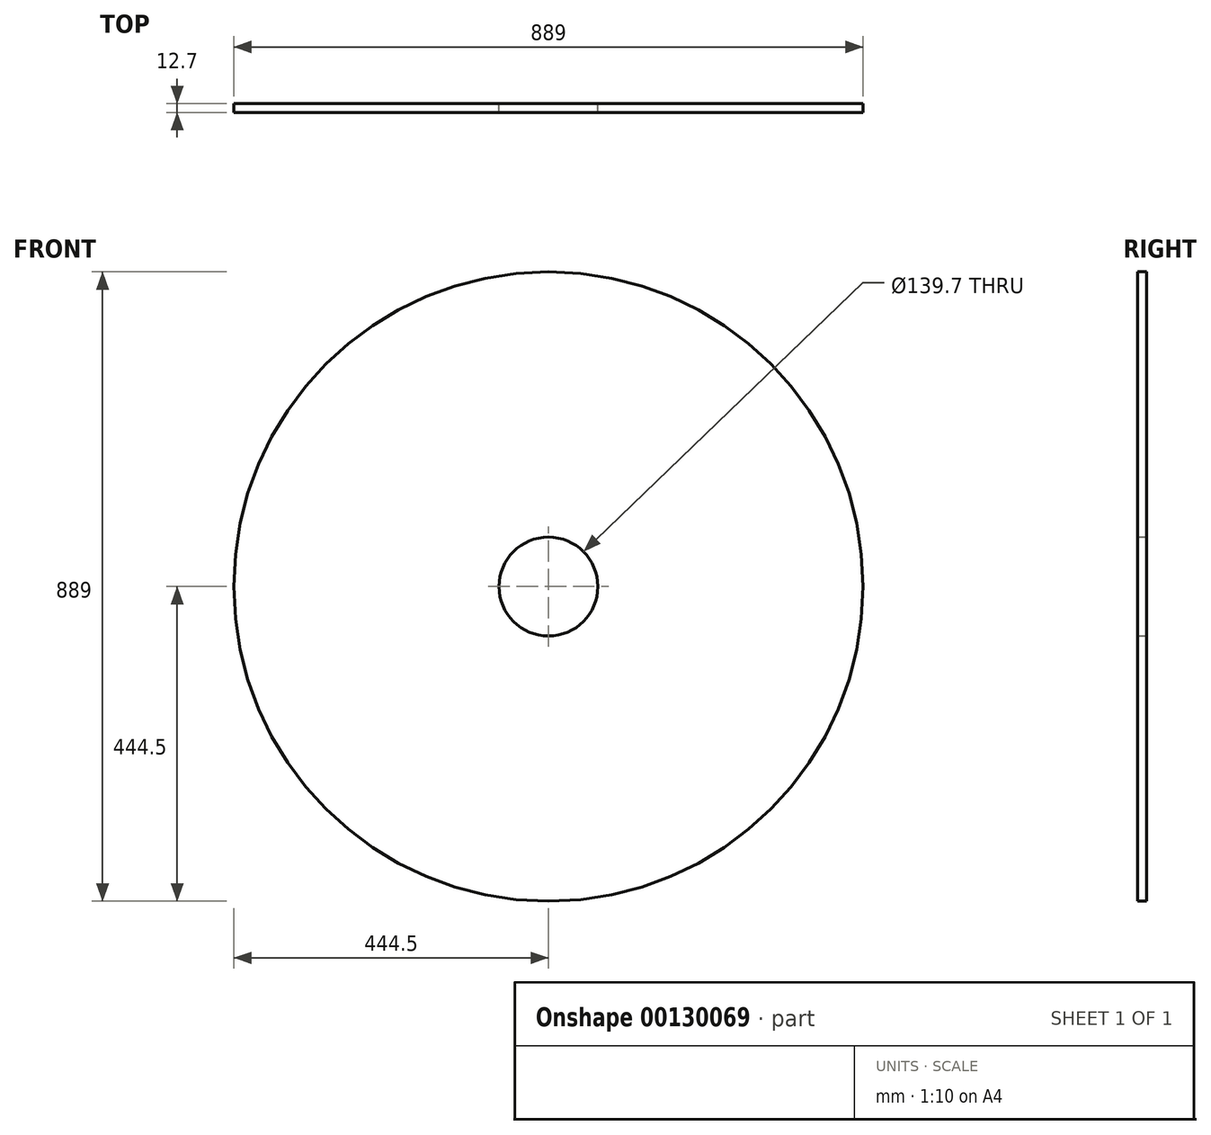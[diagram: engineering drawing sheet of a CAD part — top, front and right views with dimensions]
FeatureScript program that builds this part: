
annotation { "Feature Type Name" : "Feature", "Feature Type Description" : "" }
export const myFeature = defineFeature(function(context is Context, id is Id, definition is map)
    precondition{}
    {
        {
            var Q0;
            Q0=qCreatedBy(makeId("Front.planeOp"),FACE);
            var sketch = newSketch(context, id + "F0", { "sketchPlane" : qUnion([Q0])});
            skCircle(sketch, "E0", {"center": v(0, 0) * mm, "radius": 444.5 * mm});
            skCircle(sketch, "E1", {"center": v(0, 0) * mm, "radius": 69.85 * mm});
            skSolve(sketch);
        }
        {
            var Q0;
            Q0 = qSketchRegion(id + "F0", true);
            extrude(context, id + "F1", {"entities" : qUnion([Q0]), "depth" : 12.7 * mm});
        }
    });
